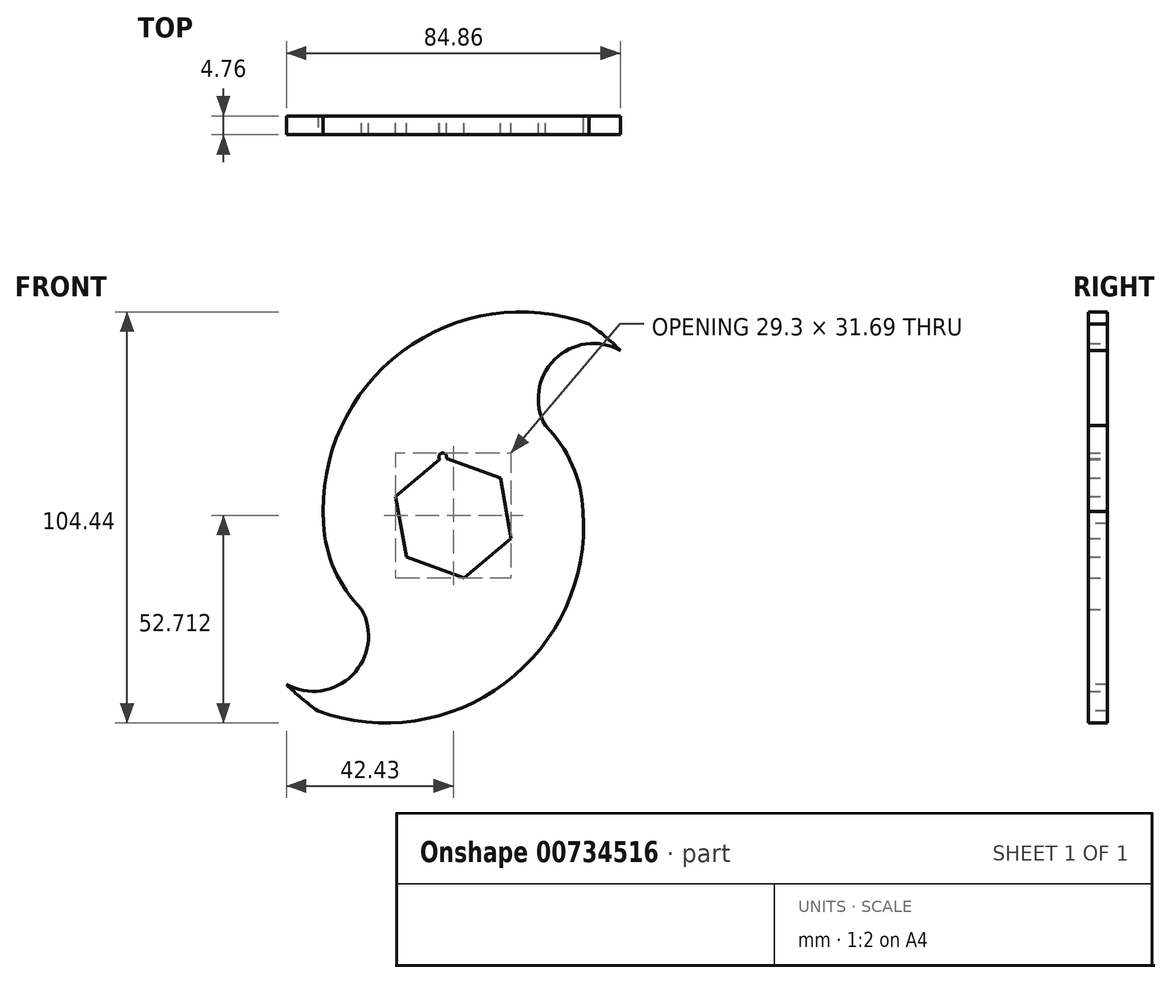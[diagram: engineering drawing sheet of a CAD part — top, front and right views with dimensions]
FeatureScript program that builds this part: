
annotation { "Feature Type Name" : "Feature", "Feature Type Description" : "" }
export const myFeature = defineFeature(function(context is Context, id is Id, definition is map)
    precondition{}
    {
        {
            var Q0;
            Q0=qCreatedBy(makeId("Front.planeOp"),FACE);
            var sketch = newSketch(context, id + "F0", { "sketchPlane" : qUnion([Q0])});
            skArc(sketch, "E0", {"start": v(-3.47, 14.7) * mm, "mid": v(-2.88, 16.34) * mm, "end": v(-1.77, 15) * mm});
            skLineSegment(sketch, "E1", {"start": v(-1.77, 15) * mm, "end": v(11.94, 10.02) * mm});
            skLineSegment(sketch, "E2", {"start": v(11.94, 10.02) * mm, "end": v(14.65, -5.33) * mm});
            skLineSegment(sketch, "E3", {"start": v(14.65, -5.33) * mm, "end": v(2.7, -15.35) * mm});
            skLineSegment(sketch, "E4", {"start": v(2.7, -15.35) * mm, "end": v(-11.94, -10.02) * mm});
            skLineSegment(sketch, "E5", {"start": v(-11.94, -10.02) * mm, "end": v(-14.65, 5.33) * mm});
            skLineSegment(sketch, "E6", {"start": v(-14.65, 5.33) * mm, "end": v(-3.47, 14.7) * mm});
            skArc(sketch, "E7", {"start": v(23.33, 23.33) * mm, "mid": v(25.68, 40.08) * mm, "end": v(42.43, 42.43) * mm});
            skArc(sketch, "E8", {"start": v(42.43, 42.43) * mm, "mid": v(38.57, 45.96) * mm, "end": v(34.43, 49.14) * mm});
            skArc(sketch, "E9", {"start": v(34.43, 49.14) * mm, "mid": v(-13.05, 42.14) * mm, "end": v(-32.97, -1.52) * mm});
            skArc(sketch, "E10", {"start": v(-32.97, -1.52) * mm, "mid": v(-30.19, -13.33) * mm, "end": v(-23.33, -23.33) * mm});
            skArc(sketch, "E11", {"start": v(-23.33, -23.33) * mm, "mid": v(-25.68, -40.08) * mm, "end": v(-42.43, -42.43) * mm});
            skArc(sketch, "E12", {"start": v(-42.43, -42.43) * mm, "mid": v(-38.57, -45.96) * mm, "end": v(-34.43, -49.14) * mm});
            skArc(sketch, "E13", {"start": v(-34.43, -49.14) * mm, "mid": v(13.05, -42.14) * mm, "end": v(32.97, 1.52) * mm});
            skArc(sketch, "E14", {"start": v(32.97, 1.52) * mm, "mid": v(30.19, 13.33) * mm, "end": v(23.33, 23.33) * mm});
            skSolve(sketch);
        }
        {
            var Q0;
            Q0 = qSketchRegion(id + "F0", true);
            extrude(context, id + "F1", {"entities" : qUnion([Q0]), "depth" : 4.76 * mm, "offsetDistance" : 25.4 * mm});
        }
    });
